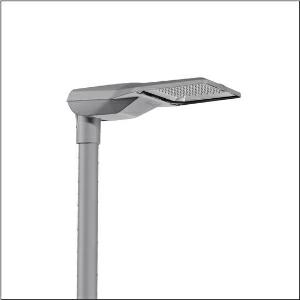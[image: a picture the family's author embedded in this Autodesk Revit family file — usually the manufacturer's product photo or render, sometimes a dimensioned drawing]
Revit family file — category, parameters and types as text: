
# Revit family: streetlight_sl_21_iq_midi___st0_5a_5xe3b41d08nb_db24
name_source: partatom
category: Lighting Fixtures
units: mm (PartAtom-declared; Revit-internal decimal feet)

## family parameters
Cut with Voids When Loaded = No
Host = Face
Light Source = No
Part Type = Normal
Room Calculation Point = No
Round Connector Dimension = Use Diameter
Shared = No

## types (1)
- --- (1 x LED, 24250 lm, 155.5 W, 4000K)
    Apparent Load = 155 VA
    CIE Flux Codes = 43 76 97 100 100
    Color Rendering = 70
    Color Temperature = 4000K
    Default Elevation = 1800 mm
    Description = Streetlight SL 21 iQ midi, mast luminaire, primary light control with lens, of PMMA, primary optical cover: cover, of toughened safety glass, transparent, light distribution: ST0.5a, light emission: direct distribution, primary light characteristic: asymmetric, installation type: post-top, side-entry, LED, High Power LED, rated luminous flux: 24.250lm, luminous efficacy: 156lm/W, light colour: 740, colour temperature: 4000K, control: Auto-Match, Temp-Guard, Lumen-Switch, Night-Set, Smart-Wire, Light-Fading, Desk-Remote (wireless, voltage-free reading and setting of iQ features in the workshop via application-optimized NFC function/RFID function), optimised constant luminous flux control (CLO 2.0), pre-setting: linear dimming characteristic, mains connection: 230..240V, AC, 50/60Hz, start of lifetime: 156W, end of service life: 162W, reduction: 69W, luminaire housing, of diecast aluminium, powder-coated, Siteco® metallic grey (DB 702S), corrosivity category C5 mid according to DIN EN ISO 12944, please order mast flange separately, inclination adjustable: 0°, 5°, 10°, 15°, sealing non-destructively replaceable, multi-level sealing system, length: 644mm, width: 335mm, height: 110mm, mast flange for spigot size: 42mm (side-entry): 5XC10008XM4, 60/48mm (side-entry/post-top): 5XC10108XM2, 76/60mm (side-entry/post-top): 5XC10108XM1, protection rating (complete): IP66, insulation class (complete): insulation class II (safety insulation), certification: CE, ENEC, ENEC+, VDE, impact resistance: IK09, permissible operating ambient temperature for outdoor applications: -40..+50°C, standard-compliant lighting for roads and squares, packaging unit: 1 piece

Light Distribution: ST0.5a
    Height = 111 mm
    Lamp = 1 x LED
    Lamp Light Flux = 24250 lm
    Lamp Power = 155.5 W
    Lamp count = 1
    Length = 644 mm
    Luminous efficacy = 156 lm/W
    Manufacturer = Siteco
    ModVariant = No
    Model = 5XE3B41D08NB
    Number of Poles = 1
    OnlyDefault = Yes
    Power Factor = 1
    Product Name = Streetlight SL 21 iQ midi | ST0.5a
    Product group = mast luminaire | pylon top
    ProductGroupID = 6100
    Protection Class = Protection class II
    Protection Degree = IP 66
    RLX_Detail_Level = 1
    RLX_Emergency_Light_Flux = 0 lm
    RLX_Emergency_Type = 0
    RLX_Emergency_Type_DB = No
    RlxData = <blob elided: 102393 chars, md5=2ba2811b>
    Socket = socket
    Standby Power = 0 W
    System Light Flux = 24250 lm
    System Power = 155 W
    Type Comments = factory setting: luminous flux: 100 % | dim-lin: 254 | 823 mA
    Type Image = l_1004298.jpg
    URL = http://relux.com
    VarID = @adj_142463
    Voltage = 0 V
    Weight = 0.00 kg
    Width = 336 mm

## geometry (parser evidence)
native form markers: Blend x4, Sweep x10
no freeform markers — native parametric forms only
